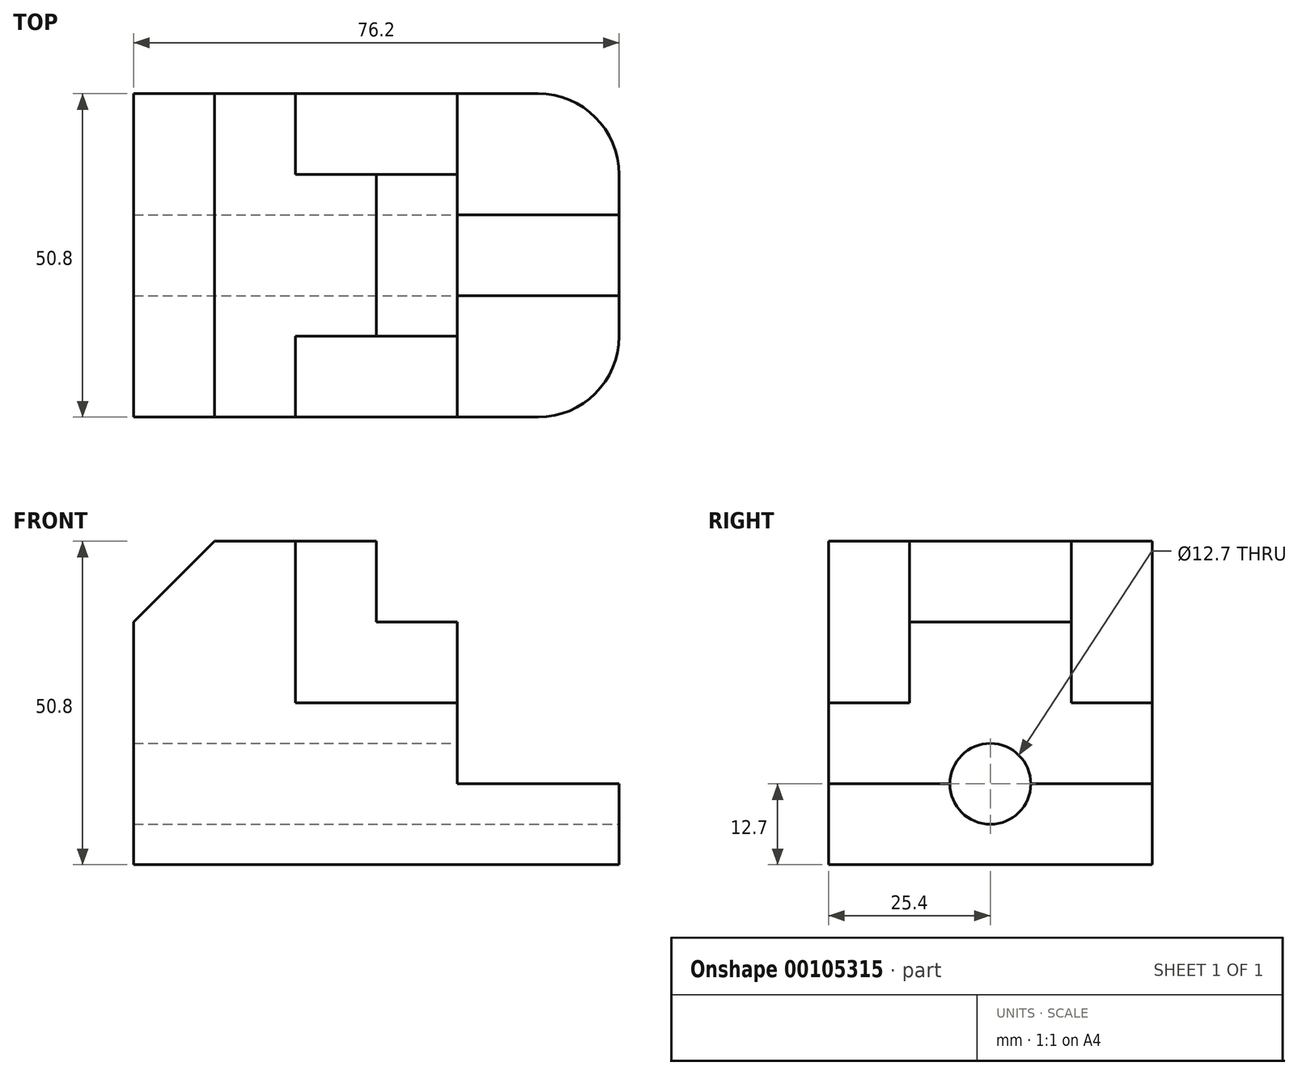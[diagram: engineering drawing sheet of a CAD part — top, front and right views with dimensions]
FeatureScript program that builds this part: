
annotation { "Feature Type Name" : "Feature", "Feature Type Description" : "" }
export const myFeature = defineFeature(function(context is Context, id is Id, definition is map)
    precondition{}
    {
        {
            var Q0;
            Q0=qCreatedBy(makeId("Front.planeOp"),FACE);
            var sketch = newSketch(context, id + "F0", { "sketchPlane" : qUnion([Q0])});
            skLineSegment(sketch, "E0", {"start": v(0, 0) * mm, "end": v(76.2, 0) * mm});
            skLineSegment(sketch, "E1", {"start": v(76.2, 0) * mm, "end": v(76.2, 12.7) * mm});
            skLineSegment(sketch, "E2", {"start": v(76.2, 12.7) * mm, "end": v(50.8, 12.7) * mm});
            skLineSegment(sketch, "E3", {"start": v(50.8, 12.7) * mm, "end": v(50.8, 25.4) * mm});
            skLineSegment(sketch, "E4", {"start": v(50.8, 25.4) * mm, "end": v(25.4, 25.4) * mm});
            skLineSegment(sketch, "E5", {"start": v(25.4, 25.4) * mm, "end": v(25.4, 50.8) * mm});
            skLineSegment(sketch, "E6", {"start": v(25.4, 50.8) * mm, "end": v(12.7, 50.8) * mm});
            skLineSegment(sketch, "E7", {"start": v(12.7, 50.8) * mm, "end": v(0, 38.1) * mm});
            skLineSegment(sketch, "E8", {"start": v(0, 38.1) * mm, "end": v(0, 0) * mm});
            skLineSegment(sketch, "E9", {"start": v(25.4, 50.8) * mm, "end": v(38.1, 50.8) * mm});
            skPoint(sketch, "E9.endSnap0", {"position": v(38.1, 25.4) * mm});
            skLineSegment(sketch, "E10", {"start": v(38.1, 50.8) * mm, "end": v(38.1, 38.1) * mm});
            skLineSegment(sketch, "E11", {"start": v(38.1, 38.1) * mm, "end": v(50.8, 38.1) * mm});
            skLineSegment(sketch, "E12", {"start": v(50.8, 38.1) * mm, "end": v(50.8, 25.4) * mm});
            skSolve(sketch);
        }
        {
            var Q0;
            Q0=makeQuery(id+"F0.imprint","IMPRINT",FACE,{"disambiguationData":[TD([[makeQuery(id+"F0.imprint","IMPRINT",EDGE,{"derivedFrom":sQuery(id+"F0.wireOp",EDGE,"E0")}),1.0]])]});
            extrude(context, id + "F1", {"entities" : qUnion([Q0]), "endBound" : BoundingType.SYMMETRIC, "depth" : 50.8 * mm});
        }
        {
            var Q0;
            Q0=makeQuery(id+"F0.imprint","IMPRINT",FACE,{"disambiguationData":[TD([[makeQuery(id+"F0.imprint","IMPRINT",EDGE,{"derivedFrom":sQuery(id+"F0.wireOp",EDGE,"E4")}),-1.0]])]});
            extrude(context, id + "F2", {"entities" : qUnion([Q0]), "operationType" : NewBodyOperationType.ADD, "endBound" : BoundingType.SYMMETRIC, "depth" : 25.4 * mm});
        }
        {
            var Q0;
            Q0=makeQuery(id+"F1.opExtrude","CAP_EDGE",EDGE,{"disambiguationData":[OSD([sQuery(id+"F0.wireOp",EDGE,"E1")])],"isStart":false});
            var Q1;
            Q1=makeQuery(id+"F1.opExtrude","CAP_EDGE",EDGE,{"disambiguationData":[OSD([sQuery(id+"F0.wireOp",EDGE,"E1")])],"isStart":true});
            fillet(context, id + "F3", {"entities" : qUnion([Q0, Q1]), "radius" : 12.7 * mm, "tangentPropagation" : true, "allowEdgeOverflow" : false});
        }
        {
            var Q0;
            Q0=makeQuery(id+"F1.opExtrude","SWEPT_FACE",FACE,{"disambiguationData":[OSD([sQuery(id+"F0.wireOp",EDGE,"E1")])]});
            var sketch = newSketch(context, id + "F4", { "sketchPlane" : qUnion([Q0])});
            skCircle(sketch, "E13", {"center": v(0, 12.7) * mm, "radius": 6.35 * mm});
            skSolve(sketch);
        }
        {
            var Q0;
            Q0 = qSketchRegion(id + "F4", true);
            extrude(context, id + "F5", {"entities" : qUnion([Q0]), "operationType" : NewBodyOperationType.REMOVE, "endBound" : BoundingType.THROUGH_ALL, "oppositeDirection" : true, "depth" : 25.4 * mm});
        }
    });
